# Revit family: BOS-Eckschutzprofil-ED-15NbED-STW_Familie
name_source: partatom
category: Türen
revit_build: Autodesk Revit 2017 (Build: 20160225_1515(x64)
units: mm (PartAtom-declared; Revit-internal decimal feet)

## family parameters
Basisbauteil = Wand
Beim Laden mit Abzugskörper schneiden = Nein
Gemeinsam genutzt = Nein
Immer vertikal = Ja
Raumberechnungspunkt = Ja

## types (2) — shared parameters
Allgemeine Informationen zu Stahlzargen = www.BestOfSteel.de/tools-downloads/technische-infos-rund-um-die-stahlzarge/
BE max. = 100 mm  [stored 0.328084 ft]
Bauelement = BOS Eckschutzprofil
Einfügepunkt = 30 mm  [stored 0.0984252 ft]
Funktion = Innen
Hersteller = BOS GmbH Best Of Steel, Lütkenfelde 4, D-48282 Emsdetten
Info-Texte sichtbar = Ja
Information in English = Nein
LDB max. = 1311 mm  [stored 4.30118 ft]
LDB min. = 561 mm
LDH max. = 2843 mm  [stored 9.32743 ft]
LDH min. = 1593 mm  [stored 5.22638 ft]
Material = grundiert, feuerverzinktes Feinblech nach DIN EN 10143
Material - Zarge = <Nach Kategorie>
Putzwinkel hinten = 15 mm  [stored 0.0492126 ft]
Putzwinkel vorne (ED) = 15 mm  [stored 0.0492126 ft]
URL = www.BestOfSteel.de/stahlzargen/weitere-loesungen/eckschutz-wandabschlussprofile/
Wandstärke min. = 125 mm  [stored 0.410105 ft]
zero-valued in all types: Breite, Dicke, Rohbaubreite, Rohbauhöhe

## per-type parameters (varying)
| type | 15NbED | Beschreibung | ED | Putzwinkel vorne |
| Eckschutzprofil ED | Nein | Eckschutzprofil ED für Ständerwerk | Ja | 15 mm  [stored 0.0492126 ft] |
| Eckschutzprofil 15NbED | Ja | Eckschutzprofil mit Schattennut für Ständerwerk | Nein | 0 mm  [stored 0 ft] |

note: column(s) folded — value = type name in every type: Modell

note: [stored X ft] marks values corroborated as IEEE doubles in the binary element streams (Revit-internal decimal feet)
